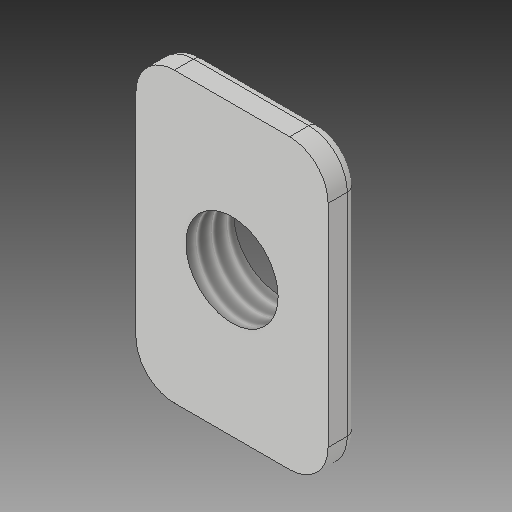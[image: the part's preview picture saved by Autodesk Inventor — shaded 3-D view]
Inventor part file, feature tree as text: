
AUTODESK INVENTOR PART (.ipt)
format: ipt  version: 2017 (Build 210142000, 142)  size: 160,256 bytes
history: native  units: mm
features: other x3, sketch x2
ambient origin geometry x8: Origin, YZ Plane, XZ Plane, XY Plane, X Axis, Y Axis, Z Axis, Center Point
bodies: Solid1 (feature_tree)
feature tree (5):
  other  "M5 Tee Nut-Generic.ipt"
  other  "Solid1::M5 Tee Nut-Generic.ipt"
  other  "TaggingFeature1"
  sketch  "Sketch1"  dims[d0=10.0mm]
  sketch  "Sketch2"
